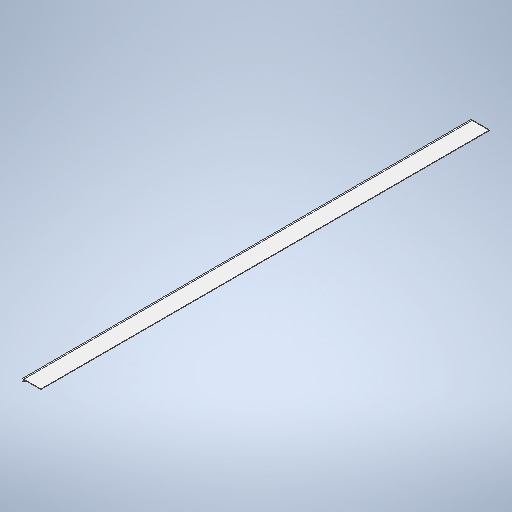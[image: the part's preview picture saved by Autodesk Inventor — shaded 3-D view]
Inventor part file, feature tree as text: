
AUTODESK INVENTOR PART (.ipt)
format: ipt  version: 2025 (Build 290162010, 162A)  size: 269,312 bytes
history: native  units: in
note: dims shown in document units (in); Inventor stores cm internally (conversion verified against a paired STEP export)
features: extrude x1, sketch x1
ambient origin geometry x8: Origin, YZ Plane, XZ Plane, XY Plane, X Axis, Y Axis, Z Axis, Center Point
bodies: Body1 (feature_tree)
feature tree (2):
  extrude  "Extrusion2"  Depth=0.125in
  sketch  "Sketch1"  dims[d49=0.125in d50=0.125in d51=0.125in d52=0.125in d54=0.333in d55=0.333in d59=146.0965in d60=0.0in d61=0.333in d62=6.0in d64=0.5in]
